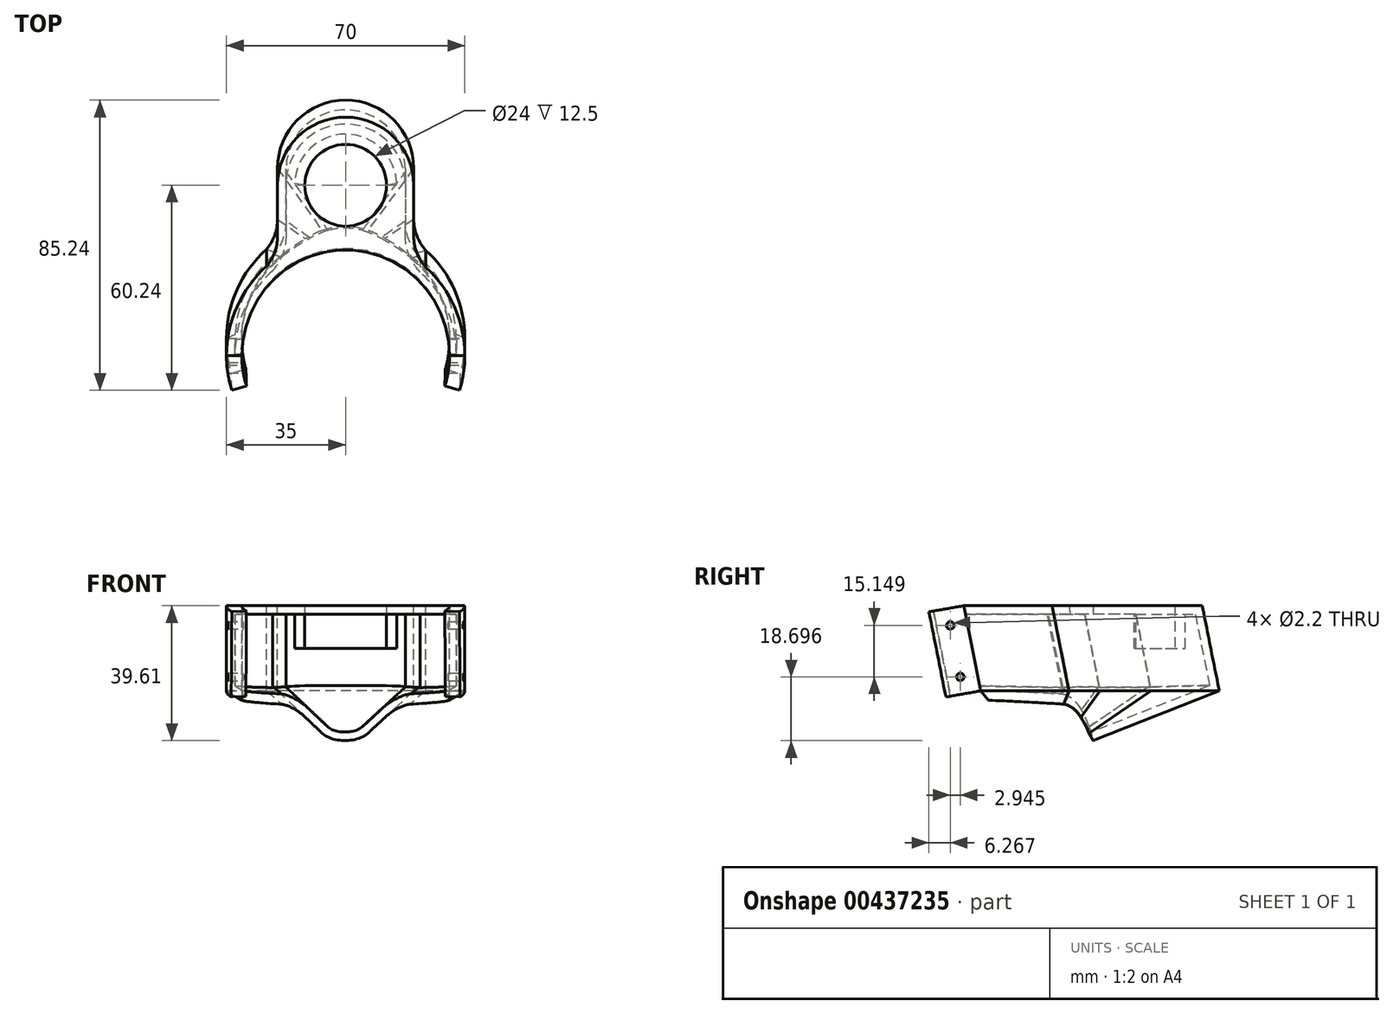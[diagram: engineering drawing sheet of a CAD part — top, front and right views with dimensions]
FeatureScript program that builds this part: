
annotation { "Feature Type Name" : "Feature", "Feature Type Description" : "" }
export const myFeature = defineFeature(function(context is Context, id is Id, definition is map)
    precondition{}
    {
        {
            var Q0;
            Q0=qCreatedBy(makeId("Top.planeOp"),FACE);
            var sketch = newSketch(context, id + "F0", { "sketchPlane" : qUnion([Q0])});
            skArc(sketch, "E0", {"start": v(35, 0) * mm, "mid": v(0, 35) * mm, "end": v(-35, 0) * mm, "construction": true});
            skLineSegment(sketch, "E1", {"start": v(-20, 50) * mm, "end": v(-20, 35) * mm});
            skLineSegment(sketch, "E2", {"start": v(20, 50) * mm, "end": v(20, 35) * mm});
            skLineSegment(sketch, "E3", {"start": v(-35, 0) * mm, "end": v(35, 0) * mm});
            skArc(sketch, "E4", {"start": v(20, 35) * mm, "mid": v(20.93, 30.1) * mm, "end": v(23.58, 25.87) * mm});
            skArc(sketch, "E5", {"start": v(20, 50) * mm, "mid": v(0, 70) * mm, "end": v(-20, 50) * mm});
            skArc(sketch, "E6", {"start": v(-23.2, 26.2) * mm, "mid": v(-20.83, 30.32) * mm, "end": v(-20, 35) * mm});
            skArc(sketch, "E7", {"start": v(-23.2, 26.2) * mm, "mid": v(-31.91, 14.37) * mm, "end": v(-35, 0) * mm});
            skArc(sketch, "E8", {"start": v(35, 0) * mm, "mid": v(32.02, 14.14) * mm, "end": v(23.58, 25.87) * mm});
            skSolve(sketch);
        }
        {
            var Q0;
            Q0=qCreatedBy(makeId("Top.planeOp"),FACE);
            cPlane(context, id + "F1", {"entities" : qUnion([Q0]), "cplaneType" : CPlaneType.OFFSET, "offset" : 25 * mm, "oppositeDirection" : true, "width" : 150 * mm, "height" : 150 * mm});
        }
        {
            var Q0;
            Q0=qCreatedBy(id+"F1.planeOp",FACE);
            var sketch = newSketch(context, id + "F2", { "sketchPlane" : qUnion([Q0])});
            skArc(sketch, "E9", {"start": v(35, 5) * mm, "mid": v(0, 40) * mm, "end": v(-35, 5) * mm, "construction": true});
            skLineSegment(sketch, "E10", {"start": v(-20, 55) * mm, "end": v(-20, 40) * mm});
            skLineSegment(sketch, "E11", {"start": v(20, 55) * mm, "end": v(20, 40) * mm});
            skLineSegment(sketch, "E12", {"start": v(-35, 5) * mm, "end": v(35, 5) * mm});
            skArc(sketch, "E13", {"start": v(20, 40) * mm, "mid": v(20.93, 35.1) * mm, "end": v(23.58, 30.87) * mm});
            skArc(sketch, "E14", {"start": v(20, 55) * mm, "mid": v(0, 75) * mm, "end": v(-20, 55) * mm});
            skArc(sketch, "E15", {"start": v(-23.2, 31.2) * mm, "mid": v(-20.83, 35.32) * mm, "end": v(-20, 40) * mm});
            skArc(sketch, "E16", {"start": v(-23.2, 31.2) * mm, "mid": v(-31.91, 19.37) * mm, "end": v(-35, 5) * mm});
            skArc(sketch, "E17", {"start": v(35, 5) * mm, "mid": v(32.02, 19.14) * mm, "end": v(23.58, 30.87) * mm});
            skSolve(sketch);
        }
        {
            var Q0;
            {var subQ0=sQuery(id+"F2.wireOp",EDGE,"E12");Q0=makeQuery(id+"F2.imprint","IMPRINT",FACE,{"disambiguationData":[TD([[makeQuery(id+"F2.imprint","IMPRINT",EDGE,{"derivedFrom":subQ0}),1.0]])]});}
            var Q1;
            {var subQ0=sQuery(id+"F0.wireOp",EDGE,"E3");Q1=makeQuery(id+"F0.imprint","IMPRINT",FACE,{"disambiguationData":[TD([[makeQuery(id+"F0.imprint","IMPRINT",EDGE,{"derivedFrom":subQ0}),1.0]])]});}
            loft(context, id + "F3", {"sheetProfilesArray" : [{ "sheetProfileEntities" : qUnion([Q0]) }, { "sheetProfileEntities" : qUnion([Q1]) }]});
        }
        {
            var Q0;
            Q0=makeQuery(id+"F2.imprint","IMPRINT",FACE,{"disambiguationData":[TD([[makeQuery(id+"F2.imprint","IMPRINT",EDGE,{"derivedFrom":sQuery(id+"F2.wireOp",EDGE,"E10")}),1.0]])]});
            var Q1;
            Q1=makeQuery(id+"F0.imprint","IMPRINT",FACE,{"disambiguationData":[TD([[makeQuery(id+"F0.imprint","IMPRINT",EDGE,{"derivedFrom":sQuery(id+"F0.wireOp",EDGE,"E1")}),1.0]])]});
            loft(context, id + "F4", {"operationType" : NewBodyOperationType.ADD, "sheetProfilesArray" : [{ "sheetProfileEntities" : qUnion([Q0]) }, { "sheetProfileEntities" : qUnion([Q1]) }]});
        }
        {
            var Q0;
            Q0=qCreatedBy(id+"F1.planeOp",FACE);
            cPlane(context, id + "F5", {"entities" : qUnion([Q0]), "cplaneType" : CPlaneType.OFFSET, "offset" : 15 * mm, "oppositeDirection" : true, "width" : 150 * mm, "height" : 150 * mm});
        }
        {
            var Q0;
            Q0=qCreatedBy(id+"F5.planeOp",FACE);
            var sketch = newSketch(context, id + "F6", { "sketchPlane" : qUnion([Q0])});
            skArc(sketch, "E18", {"start": v(10, 16.96) * mm, "mid": v(0, 26.97) * mm, "end": v(-10, 16.97) * mm, "construction": true});
            skLineSegment(sketch, "E19", {"start": v(-10, 16.97) * mm, "end": v(10, 16.96) * mm});
            skArc(sketch, "E20", {"start": v(3.79, 32.96) * mm, "mid": v(-0.21, 36.96) * mm, "end": v(-4.21, 32.96) * mm});
            skLineSegment(sketch, "E21", {"start": v(-4.21, 32.96) * mm, "end": v(-4.21, 28.96) * mm});
            skLineSegment(sketch, "E22", {"start": v(3.79, 32.96) * mm, "end": v(3.79, 28.96) * mm});
            skArc(sketch, "E23", {"start": v(-6, 24.97) * mm, "mid": v(-4.68, 26.77) * mm, "end": v(-4.21, 28.96) * mm});
            skArc(sketch, "E24", {"start": v(3.79, 28.96) * mm, "mid": v(4.38, 26.68) * mm, "end": v(6, 24.97) * mm});
            skArc(sketch, "E25", {"start": v(-6, 24.97) * mm, "mid": v(-8.94, 21.44) * mm, "end": v(-10, 16.97) * mm});
            skArc(sketch, "E26", {"start": v(10, 16.96) * mm, "mid": v(8.95, 21.44) * mm, "end": v(6, 24.97) * mm});
            skSolve(sketch);
        }
        {
            var Q1;
            Q1=makeQuery(id+"F2.imprint","IMPRINT",FACE,{"disambiguationData":[TD([[makeQuery(id+"F2.imprint","IMPRINT",EDGE,{"derivedFrom":sQuery(id+"F2.wireOp",EDGE,"E10")}),1.0]])]});
            var Q2;
            Q2=makeQuery(id+"F6.imprint","IMPRINT",FACE,{"disambiguationData":[TD([[makeQuery(id+"F6.imprint","IMPRINT",EDGE,{"derivedFrom":sQuery(id+"F6.wireOp",EDGE,"E19")}),1.0]])]});
            loft(context, id + "F7", {"operationType" : NewBodyOperationType.ADD, "sheetProfilesArray" : [{ "sheetProfileEntities" : qUnion([Q1]) }, { "sheetProfileEntities" : qUnion([Q2]) }]});
        }
        {
            var Q0;
            Q0=makeQuery(id+"F7.opLoft","SWEPT_FACE",FACE,{"disambiguationData":[OSD([sQuery(id+"F2.wireOp",EDGE,"E12"),sQuery(id+"F2.wireOp",EDGE,"E16"),sQuery(id+"F2.wireOp",EDGE,"E17"),sQuery(id+"F6.wireOp",EDGE,"E19"),sQuery(id+"F6.wireOp",EDGE,"E25"),sQuery(id+"F6.wireOp",EDGE,"E26")])]});
            var Q1;
            Q1=makeQuery(id+"F3.opLoft","SWEPT_FACE",FACE,{"disambiguationData":[OSD([sQuery(id+"F0.wireOp",EDGE,"E3"),sQuery(id+"F0.wireOp",EDGE,"E7"),sQuery(id+"F0.wireOp",EDGE,"E8"),sQuery(id+"F2.wireOp",EDGE,"E12"),sQuery(id+"F2.wireOp",EDGE,"E16"),sQuery(id+"F2.wireOp",EDGE,"E17")])]});
            shell(context, id + "F8", {"entities" : qUnion([Q0, Q1]), "thickness" : 2.5 * mm});
        }
        {
            var Q0;
            Q0=qCreatedBy(makeId("Top.planeOp"),FACE);
            var Q1;
            Q1=makeQuery(id+"F4.opLoft","MID_CAP_EDGE",EDGE,{"disambiguationData":[OSD([sQuery(id+"F0.wireOp",EDGE,"E0"),sQuery(id+"F0.wireOp",EDGE,"E3")])],"capPos":0.0});
            var Q2;
            Q2=sQuery(id+"F0.wireOp",EDGE,"E3");
            cPlane(context, id + "F9", {"entities" : qUnion([Q0, Q1, Q2]), "cplaneType" : CPlaneType.LINE_ANGLE, "offset" : 25 * mm, "angle" : 190 * degree, "width" : 150 * mm, "height" : 150 * mm});
        }
        {
            var Q0;
            Q0=qCreatedBy(id+"F9.planeOp",FACE);
            var sketch = newSketch(context, id + "F10", { "sketchPlane" : qUnion([Q0])});
            skCircle(sketch, "E27", {"center": v(0, 0) * mm, "radius": 30.5 * mm});
            skSolve(sketch);
        }
        {
            var Q0;
            Q0=makeQuery(id+"F10.imprint","IMPRINT",FACE,{"disambiguationData":[TD([[makeQuery(id+"F10.imprint","IMPRINT",EDGE,{"derivedFrom":sQuery(id+"F10.wireOp",EDGE,"E27")}),1.0]])]});
            extrude(context, id + "F11", {"entities" : qUnion([Q0]), "operationType" : NewBodyOperationType.REMOVE, "oppositeDirection" : true, "depth" : 100 * mm});
        }
        {
            var Q0;
            Q0=makeQuery(id+"F8.opShell","OFFSET_FACE",FACE,{"disambiguationData":[OSD([makeQuery(id+"F0.imprint","IMPRINT",FACE,{"disambiguationData":[TD([[makeQuery(id+"F0.imprint","IMPRINT",EDGE,{"derivedFrom":sQuery(id+"F0.wireOp",EDGE,"E1")}),1.0]])]})])]});
            var sketch = newSketch(context, id + "F12", { "sketchPlane" : qUnion([Q0])});
            skCircle(sketch, "E28", {"center": v(0, -50) * mm, "radius": 12 * mm});
            skSolve(sketch);
        }
        {
            var Q0;
            Q0=makeQuery(id+"F12.imprint","IMPRINT",FACE,{"disambiguationData":[TD([[makeQuery(id+"F12.imprint","IMPRINT",EDGE,{"derivedFrom":sQuery(id+"F12.wireOp",EDGE,"E28")}),1.0]])]});
            extrude(context, id + "F13", {"entities" : qUnion([Q0]), "operationType" : NewBodyOperationType.REMOVE, "oppositeDirection" : true, "depth" : 5 * mm});
        }
        {
            var Q0;
            Q0=qCreatedBy(id+"F9.planeOp",FACE);
            cPlane(context, id + "F14", {"entities" : qUnion([Q0]), "cplaneType" : CPlaneType.OFFSET, "offset" : 100 * mm, "oppositeDirection" : true, "width" : 150 * mm, "height" : 150 * mm});
        }
        {
            var Q0;
            Q0=qCreatedBy(id+"F14.planeOp",FACE);
            var sketch = newSketch(context, id + "F15", { "sketchPlane" : qUnion([Q0])});
            skCircle(sketch, "E29", {"center": v(0, 34) * mm, "radius": 2.5 * mm});
            skSolve(sketch);
        }
        {
            var Q0;
            Q0=makeQuery(id+"F15.imprint","IMPRINT",FACE,{"disambiguationData":[TD([[makeQuery(id+"F15.imprint","IMPRINT",EDGE,{"derivedFrom":sQuery(id+"F15.wireOp",EDGE,"E29")}),1.0]])]});
            extrude(context, id + "F16", {"entities" : qUnion([Q0]), "operationType" : NewBodyOperationType.REMOVE, "depth" : 30 * mm});
        }
        {
            var Q0;
            {var subQ3=sQuery(id+"F2.wireOp",EDGE,"E17");var subQ4=sQuery(id+"F2.wireOp",EDGE,"E13");var subQ5=sQuery(id+"F2.wireOp",EDGE,"E12");var subQ6=sQuery(id+"F2.wireOp",EDGE,"E16");var subQ7=sQuery(id+"F0.wireOp",EDGE,"E4");var subQ8=sQuery(id+"F0.wireOp",EDGE,"E3");var subQ9=sQuery(id+"F0.wireOp",EDGE,"E7");var subQ10=sQuery(id+"F0.wireOp",EDGE,"E8");Q0=makeQuery(id+"F11.boolean.opBoolean","SPLIT",FACE,{"disambiguationData":[TD([makeQuery(id+"F3.opLoft","SWEPT_FACE",FACE,{"disambiguationData":[OSD([subQ8,subQ7,subQ10,subQ5,subQ4,subQ3])]})])],"derivedFrom":makeQuery(id+"F3.opLoft","SWEPT_FACE",FACE,{"disambiguationData":[OSD([subQ8,subQ9,subQ10,subQ5,subQ6,subQ3])]})});}
            var sketch = newSketch(context, id + "F17", { "sketchPlane" : qUnion([Q0])});
            skLineSegment(sketch, "E30", {"start": v(30.5, -2.55) * mm, "end": v(30.5, 0) * mm});
            skLineSegment(sketch, "E31", {"start": v(30.5, 0) * mm, "end": v(35, 0) * mm});
            skLineSegment(sketch, "E32", {"start": v(35, 0) * mm, "end": v(35, -25.5) * mm});
            skLineSegment(sketch, "E33", {"start": v(30.5, -25.28) * mm, "end": v(30.5, -25.5) * mm});
            skLineSegment(sketch, "E34", {"start": v(30.5, -25.5) * mm, "end": v(35, -25.5) * mm});
            skLineSegment(sketch, "E35", {"start": v(30.5, -25.28) * mm, "end": v(30.5, -2.55) * mm});
            skSolve(sketch);
        }
        {
            var Q0;
            Q0=qCreatedBy(id+"F9.planeOp",FACE);
            var sketch = newSketch(context, id + "F18", { "sketchPlane" : qUnion([Q0])});
            skArc(sketch, "E36", {"start": v(33.66, 0) * mm, "mid": v(33.28, -5.06) * mm, "end": v(32.14, -10) * mm});
            skSolve(sketch);
        }
        {
            var Q0;
            Q0=qCreatedBy(id+"F9.planeOp",FACE);
            var sketch = newSketch(context, id + "F19", { "sketchPlane" : qUnion([Q0])});
            skArc(sketch, "E37", {"start": v(-33.66, 0) * mm, "mid": v(-33.28, -5.06) * mm, "end": v(-32.15, -10) * mm});
            skSolve(sketch);
        }
        {
            var Q0;
            {var subQ3=sQuery(id+"F2.wireOp",EDGE,"E16");var subQ4=sQuery(id+"F2.wireOp",EDGE,"E15");var subQ5=sQuery(id+"F2.wireOp",EDGE,"E12");var subQ6=sQuery(id+"F2.wireOp",EDGE,"E17");var subQ7=sQuery(id+"F0.wireOp",EDGE,"E3");var subQ8=sQuery(id+"F0.wireOp",EDGE,"E6");var subQ9=sQuery(id+"F0.wireOp",EDGE,"E7");var subQ10=sQuery(id+"F0.wireOp",EDGE,"E8");Q0=makeQuery(id+"F11.boolean.opBoolean","SPLIT",FACE,{"disambiguationData":[TD([makeQuery(id+"F3.opLoft","SWEPT_FACE",FACE,{"disambiguationData":[OSD([subQ7,subQ8,subQ9,subQ5,subQ4,subQ3])]})])],"derivedFrom":makeQuery(id+"F3.opLoft","SWEPT_FACE",FACE,{"disambiguationData":[OSD([subQ7,subQ9,subQ10,subQ5,subQ3,subQ6])]})});}
            var sketch = newSketch(context, id + "F20", { "sketchPlane" : qUnion([Q0])});
            skLineSegment(sketch, "E38", {"start": v(-35, -25.5) * mm, "end": v(-30.5, -25.5) * mm});
            skLineSegment(sketch, "E39", {"start": v(-30.5, -25.5) * mm, "end": v(-30.5, -25.28) * mm});
            skLineSegment(sketch, "E40", {"start": v(-30.5, -2.55) * mm, "end": v(-30.5, 0) * mm});
            skLineSegment(sketch, "E41", {"start": v(-30.5, 0) * mm, "end": v(-35, 0) * mm});
            skLineSegment(sketch, "E42", {"start": v(-35, 0) * mm, "end": v(-35, -25.5) * mm});
            skLineSegment(sketch, "E43", {"start": v(-30.5, -25.28) * mm, "end": v(-30.5, -2.55) * mm});
            skSolve(sketch);
        }
        {
            var Q0;
            Q0 = qSketchRegion(id + "F17", true);
            var Q1;
            Q1 = qConstructionFilter(qBodyType(qCreatedBy(id + "F18" ,EDGE), BodyType.WIRE), ConstructionObject.NO);
            sweep(context, id + "F21", {"operationType" : NewBodyOperationType.ADD, "profiles" : qUnion([Q0]), "path" : qUnion([Q1])});
        }
        {
            var Q0;
            Q0 = qSketchRegion(id + "F20", true);
            var Q1;
            Q1 = qConstructionFilter(qBodyType(qCreatedBy(id + "F19" ,EDGE), BodyType.WIRE), ConstructionObject.NO);
            sweep(context, id + "F22", {"operationType" : NewBodyOperationType.ADD, "profiles" : qUnion([Q0]), "path" : qUnion([Q1])});
        }
        {
            var Q0;
            Q0=makeQuery(id+"F8.opShell","OFFSET_FACE",FACE,{"disambiguationData":[OSD([makeQuery(id+"F0.imprint","IMPRINT",FACE,{"disambiguationData":[TD([[makeQuery(id+"F0.imprint","IMPRINT",EDGE,{"derivedFrom":sQuery(id+"F0.wireOp",EDGE,"E1")}),1.0]])]})])]});
            var sketch = newSketch(context, id + "F23", { "sketchPlane" : qUnion([Q0])});
            skArc(sketch, "E44", {"start": v(-15, -50.5) * mm, "mid": v(0, -65) * mm, "end": v(15, -50.5) * mm});
            skArc(sketch, "E45", {"start": v(12, -50) * mm, "mid": v(0, -62) * mm, "end": v(-12, -50) * mm});
            skLineSegment(sketch, "E46", {"start": v(15, -50.5) * mm, "end": v(12, -50) * mm});
            skLineSegment(sketch, "E47", {"start": v(-12, -50) * mm, "end": v(-15, -50.5) * mm});
            skSolve(sketch);
        }
        {
            var Q0;
            Q0=makeQuery(id+"F23.imprint","IMPRINT",FACE,{"disambiguationData":[TD([[makeQuery(id+"F23.imprint","IMPRINT",EDGE,{"derivedFrom":sQuery(id+"F23.wireOp",EDGE,"E44")}),1.0]])]});
            extrude(context, id + "F24", {"entities" : qUnion([Q0]), "operationType" : NewBodyOperationType.ADD, "depth" : 10 * mm});
        }
        {
            var Q0;
            Q0=qCreatedBy(makeId("Right.planeOp"),FACE);
            cPlane(context, id + "F25", {"entities" : qUnion([Q0]), "cplaneType" : CPlaneType.OFFSET, "offset" : 50 * mm, "width" : 150 * mm, "height" : 150 * mm});
        }
        {
            var Q0;
            Q0=qCreatedBy(id+"F25.planeOp",FACE);
            var sketch = newSketch(context, id + "F26", { "sketchPlane" : qUnion([Q0])});
            skCircle(sketch, "E48", {"center": v(-1.03, -20.91) * mm, "radius": 1.1 * mm});
            skCircle(sketch, "E49", {"center": v(-3.97, -5.77) * mm, "radius": 1.1 * mm});
            skLineSegment(sketch, "E50", {"start": v(4.89, -25.14) * mm, "end": v(0, 0) * mm});
            skLineSegment(sketch, "E51", {"start": v(10.52, 0) * mm, "end": v(-11.15, 0) * mm});
            skSolve(sketch);
        }
        {
            var Q0;
            Q0=makeQuery(id+"F26.imprint","IMPRINT",FACE,{"disambiguationData":[TD([[makeQuery(id+"F26.imprint","IMPRINT",EDGE,{"derivedFrom":sQuery(id+"F26.wireOp",EDGE,"E48")}),1.0]])]});
            var Q1;
            Q1=makeQuery(id+"F26.imprint","IMPRINT",FACE,{"disambiguationData":[TD([[makeQuery(id+"F26.imprint","IMPRINT",EDGE,{"derivedFrom":sQuery(id+"F26.wireOp",EDGE,"E49")}),1.0]])]});
            extrude(context, id + "F27", {"entities" : qUnion([Q0, Q1]), "operationType" : NewBodyOperationType.REMOVE, "endBound" : BoundingType.THROUGH_ALL, "oppositeDirection" : true, "depth" : 25 * mm});
        }
    });
